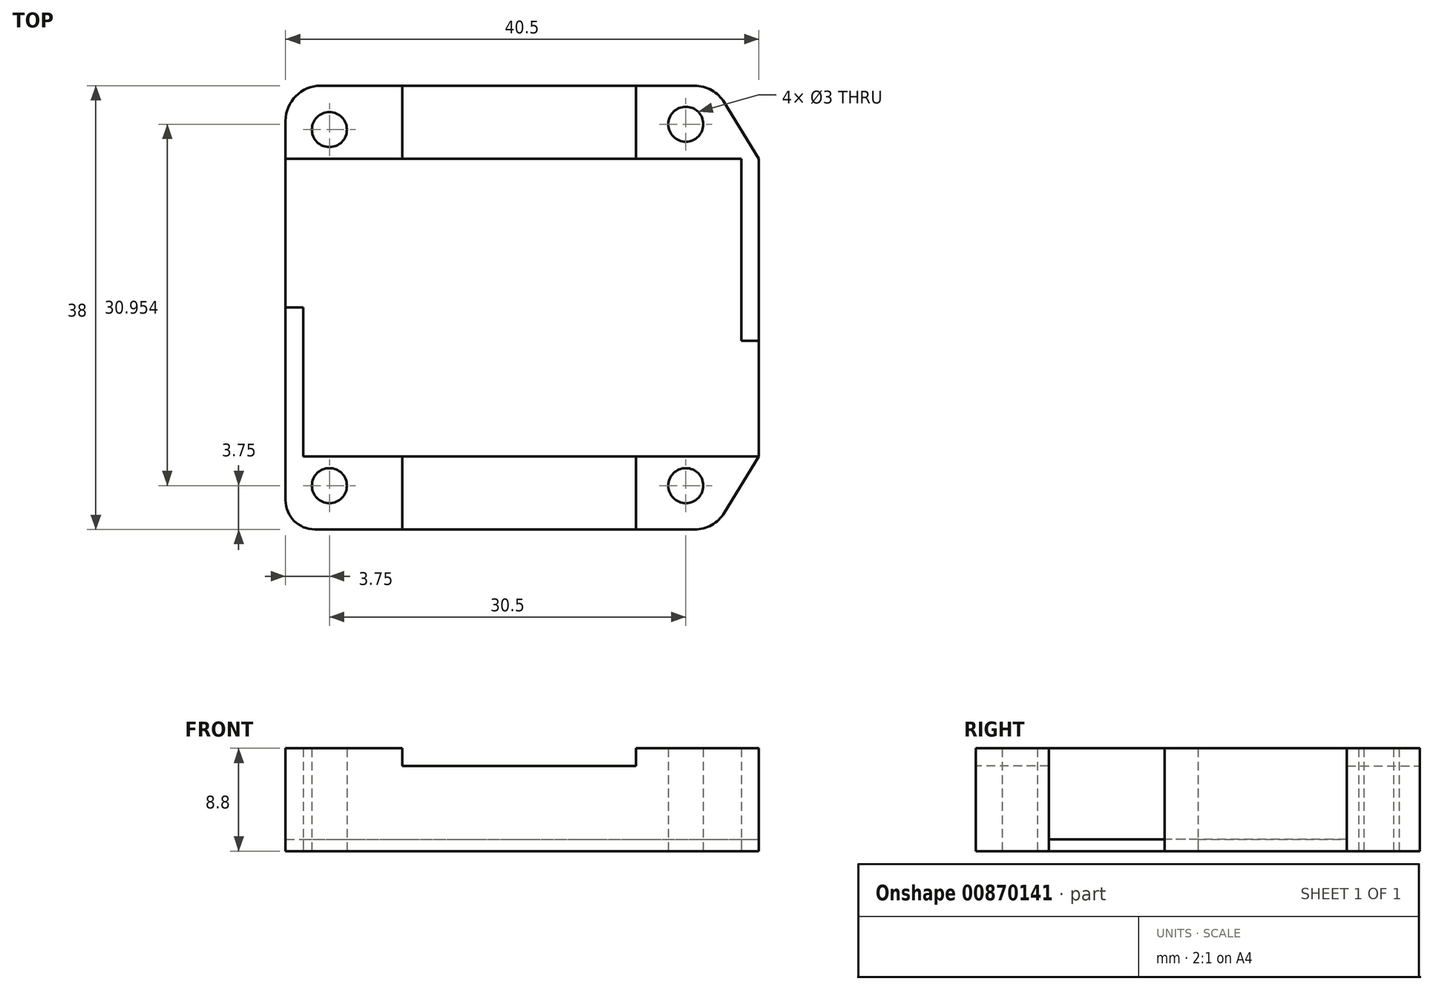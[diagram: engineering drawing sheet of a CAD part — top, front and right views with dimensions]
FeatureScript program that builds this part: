
annotation { "Feature Type Name" : "Feature", "Feature Type Description" : "" }
export const myFeature = defineFeature(function(context is Context, id is Id, definition is map)
    precondition{}
    {
        {
            var Q0;
            Q0=qCreatedBy(makeId("Top.planeOp"),FACE);
            var sketch = newSketch(context, id + "F0", { "sketchPlane" : qUnion([Q0])});
            skLineSegment(sketch, "E0.bottom", {"start": v(16, -19) * mm, "end": v(-16.5, -19) * mm});
            skLineSegment(sketch, "E0.top", {"start": v(16, 19) * mm, "end": v(-16, 19) * mm});
            skLineSegment(sketch, "E0.right", {"start": v(-19, -16.5) * mm, "end": v(-19, 16) * mm});
            skPoint(sketch, "E0.middle", {"position": v(0, 0) * mm});
            skPoint(sketch, "E1", {"position": v(15.25, 15.7) * mm});
            skPoint(sketch, "E2", {"position": v(15.25, -15.25) * mm});
            skPoint(sketch, "E3", {"position": v(-15.25, -15.25) * mm});
            skPoint(sketch, "E4", {"position": v(-15.25, 15.25) * mm});
            skCircle(sketch, "E5", {"center": v(-15.25, 15.25) * mm, "radius": 1.5 * mm});
            skCircle(sketch, "E6", {"center": v(15.25, 15.7) * mm, "radius": 1.5 * mm});
            skCircle(sketch, "E7", {"center": v(15.25, -15.25) * mm, "radius": 1.5 * mm});
            skCircle(sketch, "E8", {"center": v(-15.25, -15.25) * mm, "radius": 1.5 * mm});
            skPoint(sketch, "E9.visualSharp", {"position": v(-19, 19) * mm});
            skArc(sketch, "E9.filletArc", {"start": v(-16, 19) * mm, "mid": v(-18.12, 18.12) * mm, "end": v(-19, 16) * mm});
            skPoint(sketch, "E10.visualSharp", {"position": v(19, 19) * mm});
            skArc(sketch, "E10.filletArc", {"start": v(18.56, 17.56) * mm, "mid": v(17.47, 18.62) * mm, "end": v(16, 19) * mm});
            skPoint(sketch, "E11.visualSharp", {"position": v(19, -19) * mm});
            skArc(sketch, "E11.filletArc", {"start": v(16, -19) * mm, "mid": v(17.47, -18.62) * mm, "end": v(18.56, -17.56) * mm});
            skPoint(sketch, "E12.visualSharp", {"position": v(-19, -19) * mm});
            skArc(sketch, "E12.filletArc", {"start": v(-19, -16.5) * mm, "mid": v(-18.27, -18.27) * mm, "end": v(-16.5, -19) * mm});
            skLineSegment(sketch, "E13", {"start": v(-17.5, 12.75) * mm, "end": v(20, 12.75) * mm});
            skLineSegment(sketch, "E14", {"start": v(-17.5, -12.75) * mm, "end": v(20, -12.75) * mm});
            skLineSegment(sketch, "E15", {"start": v(21.5, 12.75) * mm, "end": v(21.5, -12.75) * mm});
            skLineSegment(sketch, "E16", {"start": v(-17.5, 12.75) * mm, "end": v(-17.5, -12.75) * mm});
            skPoint(sketch, "E17", {"position": v(20, 12.75) * mm});
            skLineSegment(sketch, "E18", {"start": v(20, 12.75) * mm, "end": v(20, -12.75) * mm});
            skLineSegment(sketch, "E19", {"start": v(21.5, 12.75) * mm, "end": v(18.56, 17.56) * mm});
            skLineSegment(sketch, "E20", {"start": v(21.5, -12.75) * mm, "end": v(18.56, -17.56) * mm});
            skPoint(sketch, "E21.orphan", {"position": v(-19, 12.75) * mm});
            skPoint(sketch, "E22.orphan", {"position": v(-19, -12.75) * mm});
            skLineSegment(sketch, "E23.bottom", {"start": v(20, -12.75) * mm, "end": v(21.5, -12.75) * mm});
            skLineSegment(sketch, "E23.top", {"start": v(20, -2.83) * mm, "end": v(21.5, -2.83) * mm});
            skLineSegment(sketch, "E23.left", {"start": v(20, -12.75) * mm, "end": v(20, -2.83) * mm});
            skLineSegment(sketch, "E23.right", {"start": v(21.5, -12.75) * mm, "end": v(21.5, -2.83) * mm});
            skLineSegment(sketch, "E24.bottom", {"start": v(-19, 12.75) * mm, "end": v(-17.5, 12.75) * mm});
            skLineSegment(sketch, "E24.top", {"start": v(-19, 0) * mm, "end": v(-17.5, 0) * mm});
            skLineSegment(sketch, "E24.left", {"start": v(-19, 12.75) * mm, "end": v(-19, 0) * mm});
            skLineSegment(sketch, "E24.right", {"start": v(-17.5, 12.75) * mm, "end": v(-17.5, 0) * mm});
            skLineSegment(sketch, "E25.bottom", {"start": v(21.5, -2.83) * mm, "end": v(29.5, -2.83) * mm});
            skLineSegment(sketch, "E25.top", {"start": v(21.5, -12.67) * mm, "end": v(29.5, -12.67) * mm});
            skLineSegment(sketch, "E25.left", {"start": v(21.5, -2.83) * mm, "end": v(21.5, -12.67) * mm});
            skLineSegment(sketch, "E25.right", {"start": v(29.5, -2.83) * mm, "end": v(29.5, -12.67) * mm});
            skLineSegment(sketch, "E26.bottom", {"start": v(23.72, -2.83) * mm, "end": v(27.8, -2.83) * mm});
            skLineSegment(sketch, "E26.top", {"start": v(23.72, -3.98) * mm, "end": v(27.8, -3.98) * mm});
            skLineSegment(sketch, "E26.left", {"start": v(23.72, -2.83) * mm, "end": v(23.72, -3.98) * mm});
            skLineSegment(sketch, "E26.right", {"start": v(27.8, -2.83) * mm, "end": v(27.8, -3.98) * mm});
            skSolve(sketch);
        }
        {
            var Q0;
            Q0=makeQuery(id+"F0.imprint","IMPRINT",FACE,{"disambiguationData":[TD([[makeQuery(id+"F0.imprint","IMPRINT",EDGE,{"derivedFrom":sQuery(id+"F0.wireOp",EDGE,"tZOkOwAx-xhKL-W8XJ-n9Dq-FD7eferK8f0z")}),-1.0]])]});
            var Q1;
            Q1=makeQuery(id+"F0.imprint","IMPRINT",FACE,{"disambiguationData":[TD([[makeQuery(id+"F0.imprint","IMPRINT",EDGE,{"derivedFrom":sQuery(id+"F0.wireOp",EDGE,"E8")}),-1.0]])]});
            var Q2;
            Q2=makeQuery(id+"F0.imprint","IMPRINT",FACE,{"disambiguationData":[TD([[makeQuery(id+"F0.imprint","IMPRINT",EDGE,{"derivedFrom":sQuery(id+"F0.wireOp",EDGE,"E7")}),-1.0]])]});
            var Q3;
            Q3=makeQuery(id+"F0.imprint","IMPRINT",FACE,{"disambiguationData":[TD([[makeQuery(id+"F0.imprint","IMPRINT",EDGE,{"derivedFrom":sQuery(id+"F0.wireOp",EDGE,"E6")}),-1.0]])]});
            var Q4;
            Q4=makeQuery(id+"F0.imprint","IMPRINT",FACE,{"disambiguationData":[TD([[makeQuery(id+"F0.imprint","IMPRINT",EDGE,{"derivedFrom":sQuery(id+"F0.wireOp",EDGE,"E5")}),-1.0]])]});
            extrude(context, id + "F1", {"entities" : qUnion([Q0, Q1, Q2, Q3, Q4]), "depth" : 8.8 * mm, "offsetDistance" : 25 * mm});
        }
        {
            var Q0;
            Q0=makeQuery(id+"F0.imprint","IMPRINT",FACE,{"disambiguationData":[TD([[makeQuery(id+"F0.imprint","IMPRINT",EDGE,{"derivedFrom":sQuery(id+"F0.wireOp",EDGE,"E8")}),-1.0]])]});
            var Q1;
            Q1=makeQuery(id+"F0.imprint","IMPRINT",FACE,{"disambiguationData":[TD([[makeQuery(id+"F0.imprint","IMPRINT",EDGE,{"derivedFrom":sQuery(id+"F0.wireOp",EDGE,"E7")}),-1.0]])]});
            var Q2;
            Q2=makeQuery(id+"F0.imprint","IMPRINT",FACE,{"disambiguationData":[TD([[makeQuery(id+"F0.imprint","IMPRINT",EDGE,{"derivedFrom":sQuery(id+"F0.wireOp",EDGE,"E6")}),-1.0]])]});
            var Q3;
            Q3=makeQuery(id+"F0.imprint","IMPRINT",FACE,{"disambiguationData":[TD([[makeQuery(id+"F0.imprint","IMPRINT",EDGE,{"derivedFrom":sQuery(id+"F0.wireOp",EDGE,"E5")}),-1.0]])]});
            extrude(context, id + "F2", {"entities" : qUnion([Q0, Q1, Q2, Q3]), "operationType" : NewBodyOperationType.ADD, "depth" : 5 * mm, "offsetDistance" : 25 * mm});
        }
        {
            var Q0;
            Q0=makeQuery(id+"F0.imprint","IMPRINT",FACE,{"disambiguationData":[TD([[makeQuery(id+"F0.imprint","IMPRINT",EDGE,{"derivedFrom":sQuery(id+"F0.wireOp",EDGE,"E13")}),-1.0]])]});
            var Q1;
            Q1=makeQuery(id+"F0.imprint","IMPRINT",FACE,{"disambiguationData":[TD([[makeQuery(id+"F0.imprint","IMPRINT",EDGE,{"derivedFrom":sQuery(id+"F0.wireOp",EDGE,"E24.bottom")}),-1.0]])]});
            var Q2;
            Q2=makeQuery(id+"F0.imprint","IMPRINT",FACE,{"disambiguationData":[TD([[makeQuery(id+"F0.imprint","IMPRINT",EDGE,{"derivedFrom":sQuery(id+"F0.wireOp",EDGE,"E23.bottom")}),1.0]])]});
            extrude(context, id + "F3", {"entities" : qUnion([Q0, Q1, Q2]), "depth" : 1 * mm, "offsetDistance" : 25 * mm});
        }
        {
            var Q0;
            Q0=makeQuery(id+"F1.opExtrude","CAP_FACE",FACE,{"disambiguationData":[OSD([sQuery(id+"F0.wireOp",EDGE,"E0.top"),sQuery(id+"F0.wireOp",EDGE,"E0.right"),sQuery(id+"F0.wireOp",EDGE,"E5"),sQuery(id+"F0.wireOp",EDGE,"E6"),sQuery(id+"F0.wireOp",EDGE,"E9.filletArc"),sQuery(id+"F0.wireOp",EDGE,"E10.filletArc"),sQuery(id+"F0.wireOp",EDGE,"E13"),sQuery(id+"F0.wireOp",EDGE,"E15"),sQuery(id+"F0.wireOp",EDGE,"E18"),sQuery(id+"F0.wireOp",EDGE,"E19"),sQuery(id+"F0.wireOp",EDGE,"E23.top"),sQuery(id+"F0.wireOp",EDGE,"E24.bottom")])],"isStart":false});
            var sketch = newSketch(context, id + "F4", { "sketchPlane" : qUnion([Q0])});
            skLineSegment(sketch, "E27.bottom", {"start": v(-9, 12.75) * mm, "end": v(11, 12.75) * mm});
            skLineSegment(sketch, "E27.top", {"start": v(-9, 19) * mm, "end": v(11, 19) * mm});
            skLineSegment(sketch, "E27.left", {"start": v(-9, 12.75) * mm, "end": v(-9, 19) * mm});
            skLineSegment(sketch, "E27.right", {"start": v(11, 12.75) * mm, "end": v(11, 19) * mm});
            skLineSegment(sketch, "E28.bottom", {"start": v(-9, -12.57) * mm, "end": v(11, -12.57) * mm});
            skLineSegment(sketch, "E28.top", {"start": v(-9, -19.01) * mm, "end": v(11, -19.01) * mm});
            skLineSegment(sketch, "E28.left", {"start": v(-9, -12.57) * mm, "end": v(-9, -19.01) * mm});
            skLineSegment(sketch, "E28.right", {"start": v(11, -12.57) * mm, "end": v(11, -19.01) * mm});
            skSolve(sketch);
        }
        {
            var Q0;
            Q0=makeQuery(id+"F4.imprint","IMPRINT",FACE,{"disambiguationData":[TD([[makeQuery(id+"F4.imprint","IMPRINT",EDGE,{"derivedFrom":sQuery(id+"F4.wireOp",EDGE,"E27.bottom")}),1.0]])]});
            var Q1;
            Q1=makeQuery(id+"F4.imprint","IMPRINT",FACE,{"disambiguationData":[TD([[makeQuery(id+"F4.imprint","IMPRINT",EDGE,{"derivedFrom":sQuery(id+"F4.wireOp",EDGE,"E28.bottom")}),-1.0]])]});
            extrude(context, id + "F5", {"entities" : qUnion([Q0, Q1]), "operationType" : NewBodyOperationType.REMOVE, "oppositeDirection" : true, "depth" : 1.5 * mm, "offsetDistance" : 25 * mm});
        }
    });
